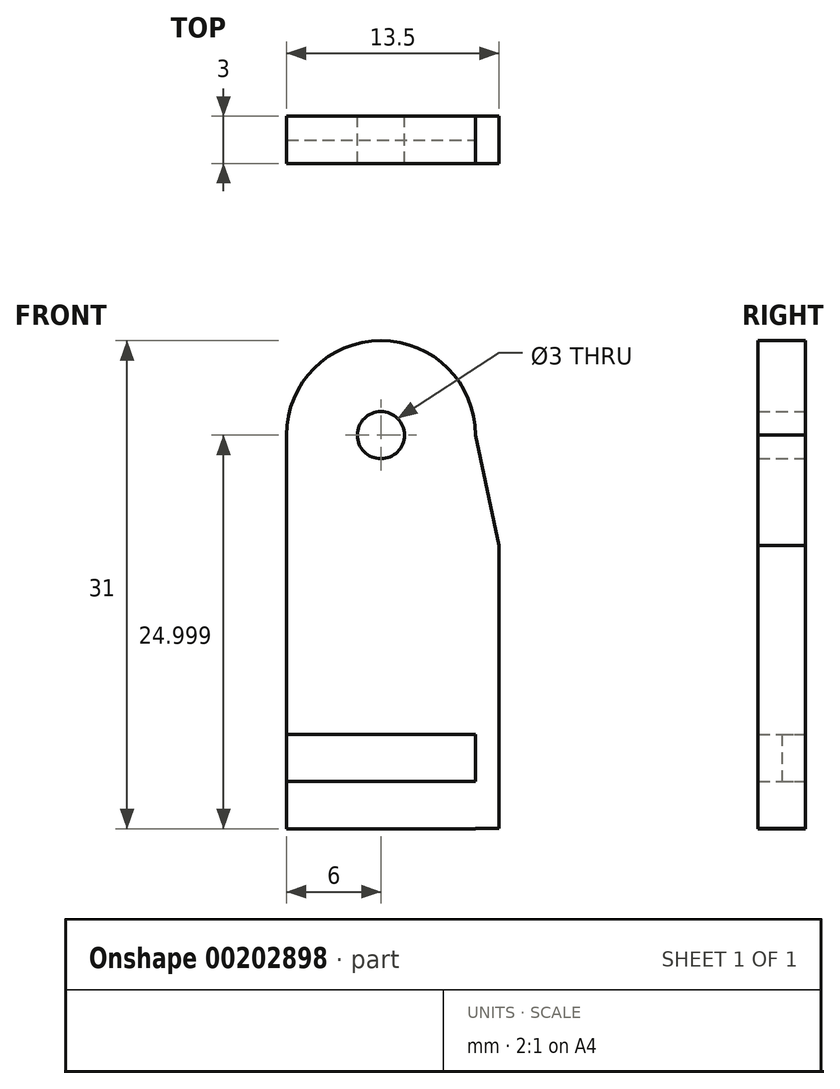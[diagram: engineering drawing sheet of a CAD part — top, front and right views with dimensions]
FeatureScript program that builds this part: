
annotation { "Feature Type Name" : "Feature", "Feature Type Description" : "" }
export const myFeature = defineFeature(function(context is Context, id is Id, definition is map)
    precondition{}
    {
        {
            var Q0;
            Q0=qCreatedBy(makeId("Front.planeOp"),FACE);
            var sketch = newSketch(context, id + "F0", { "sketchPlane" : qUnion([Q0])});
            skLineSegment(sketch, "E0", {"start": v(-49.52, 0) * mm, "end": v(53.2, 0) * mm, "construction": true});
            skLineSegment(sketch, "E1", {"start": v(0, 54.81) * mm, "end": v(0, -48.53) * mm, "construction": true});
            skLineSegment(sketch, "E2", {"start": v(-6, 0) * mm, "end": v(-6, -12.27) * mm});
            skLineSegment(sketch, "E3", {"start": v(-6, -12.27) * mm, "end": v(0, -12.27) * mm});
            skLineSegment(sketch, "E4", {"start": v(-6, -9.27) * mm, "end": v(0, -9.27) * mm});
            skLineSegment(sketch, "E5", {"start": v(-6, -6.27) * mm, "end": v(0, -6.27) * mm});
            skLineSegment(sketch, "E6", {"start": v(-6, 0) * mm, "end": v(-6, 12.73) * mm});
            skLineSegment(sketch, "E7.MirrorCS", {"start": v(6, -6.27) * mm, "end": v(6, -9.27) * mm});
            skLineSegment(sketch, "E8.MirrorCS", {"start": v(6, -6.27) * mm, "end": v(0, -6.27) * mm});
            skLineSegment(sketch, "E9.MirrorCS", {"start": v(6, -9.27) * mm, "end": v(0, -9.27) * mm});
            skLineSegment(sketch, "E10.MirrorCS", {"start": v(6, -12.27) * mm, "end": v(0, -12.27) * mm});
            skArc(sketch, "E11", {"start": v(6, 12.73) * mm, "mid": v(0, 18.73) * mm, "end": v(-6, 12.73) * mm});
            skCircle(sketch, "E12", {"center": v(0, 32.21) * mm, "radius": 1.5 * mm});
            skLineSegment(sketch, "E13", {"start": v(-7.38, 12.73) * mm, "end": v(9.04, 12.73) * mm, "construction": true});
            skCircle(sketch, "E14", {"center": v(0, 12.73) * mm, "radius": 1.5 * mm});
            skLineSegment(sketch, "E15.top", {"start": v(6, -12.26) * mm, "end": v(7.5, -12.26) * mm});
            skLineSegment(sketch, "E15.right", {"start": v(7.5, -6.27) * mm, "end": v(7.5, -12.26) * mm});
            skLineSegment(sketch, "E16.trimOffspring", {"start": v(6, -12.26) * mm, "end": v(6, -12.27) * mm});
            skPoint(sketch, "E17.orphan", {"position": v(6, 0) * mm});
            skLineSegment(sketch, "E18", {"start": v(-8.66, 5.73) * mm, "end": v(10.96, 5.73) * mm, "construction": true});
            skLineSegment(sketch, "E19", {"start": v(7.5, -6.27) * mm, "end": v(7.5, 5.73) * mm});
            skLineSegment(sketch, "E20", {"start": v(7.5, 5.73) * mm, "end": v(6, 12.73) * mm});
            skSolve(sketch);
        }
        {
            var Q0;
            {var subQ3=sQuery(id+"F0.wireOp",EDGE,"E3");Q0=makeQuery(id+"F0.imprint","IMPRINT",FACE,{"disambiguationData":[TD([[makeQuery(id+"F0.imprint","IMPRINT",EDGE,{"derivedFrom":subQ3}),1.0]])]});}
            var Q1;
            {var subQ2=sQuery(id+"F0.wireOp",EDGE,"E5");Q1=makeQuery(id+"F0.imprint","IMPRINT",FACE,{"disambiguationData":[TD([[makeQuery(id+"F0.imprint","IMPRINT",EDGE,{"derivedFrom":subQ2}),1.0]])]});}
            extrude(context, id + "F1", {"entities" : qUnion([Q0, Q1]), "depth" : 3 * mm});
        }
        {
            var Q0;
            {var subQ4=sQuery(id+"F0.wireOp",EDGE,"E4");Q0=makeQuery(id+"F0.imprint","IMPRINT",FACE,{"disambiguationData":[TD([[makeQuery(id+"F0.imprint","IMPRINT",EDGE,{"derivedFrom":subQ4}),1.0]])]});}
            extrude(context, id + "F2", {"entities" : qUnion([Q0]), "depth" : 1.5 * mm});
        }
    });
